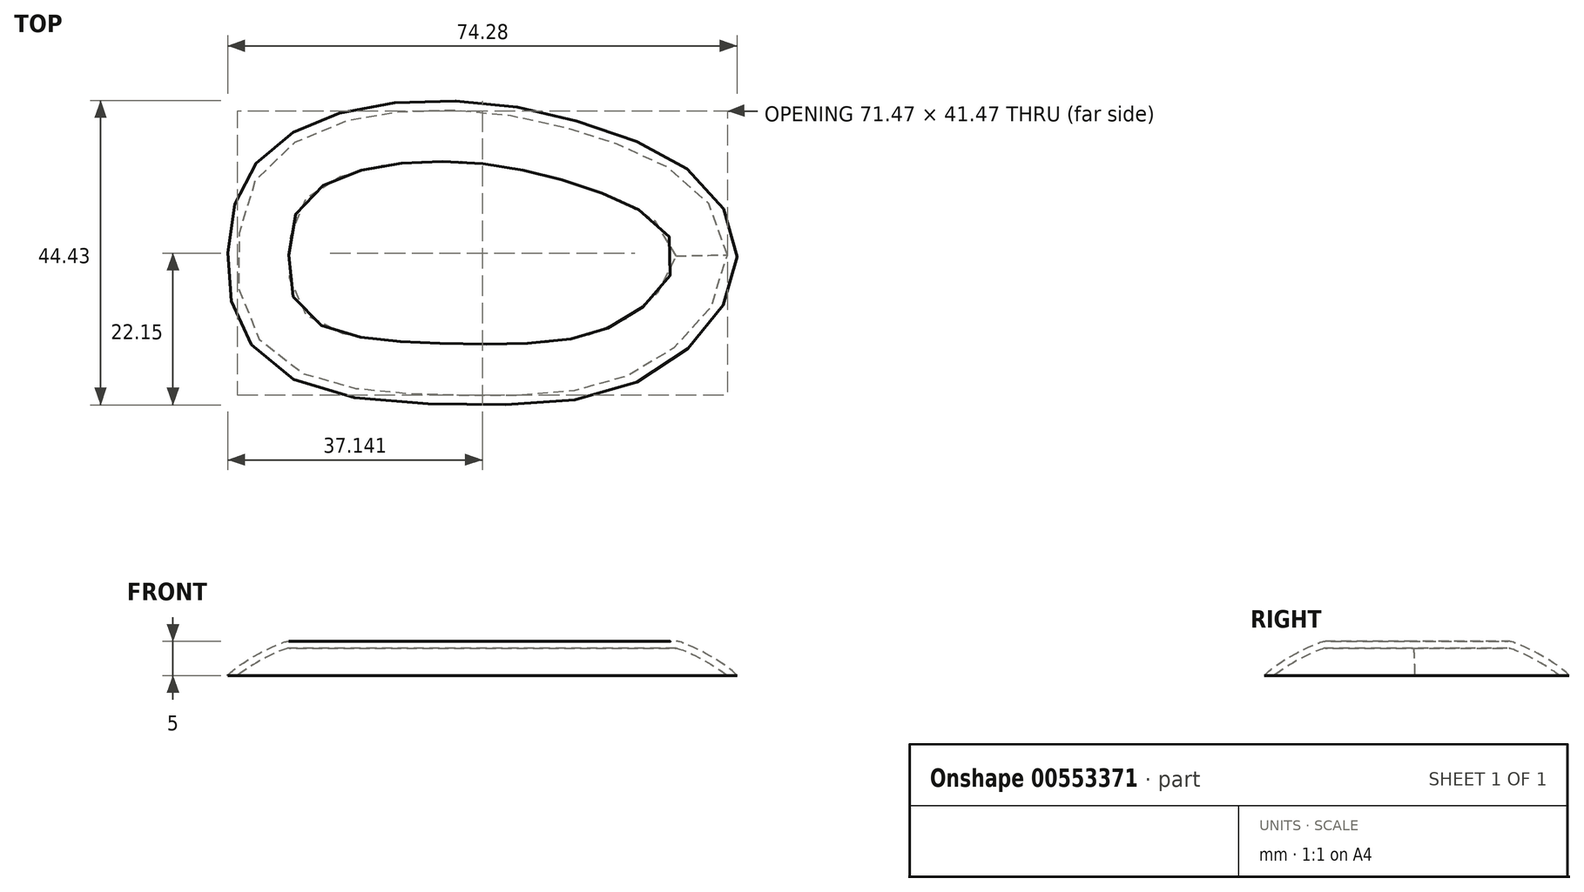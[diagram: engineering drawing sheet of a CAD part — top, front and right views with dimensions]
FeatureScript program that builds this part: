
annotation { "Feature Type Name" : "Feature", "Feature Type Description" : "" }
export const myFeature = defineFeature(function(context is Context, id is Id, definition is map)
    precondition{}
    {
        {
            var Q0;
            Q0=qCreatedBy(makeId("Top.planeOp"),FACE);
            var sketch = newSketch(context, id + "F0", { "sketchPlane" : qUnion([Q0])});
            skFitSpline(sketch, "E0", {"points": [v(0, 0) * mm, v(2.22, 10.29) * mm, v(9.49, 17.56) * mm, v(21.2, 21.46) * mm, v(38.04, 21.82) * mm, v(55.07, 17.91) * mm, v(68.9, 10.64) * mm, v(74.23, 0) * mm, v(69.97, -11) * mm, v(56.14, -20.22) * mm, v(33.61, -22.17) * mm, v(10.9, -19.16) * mm, v(1.5, -10.29) * mm, v(0, 0) * mm]});
            skSolve(sketch);
        }
        {
            var Q0;
            Q0=makeQuery(id+"F0.imprint","IMPRINT",FACE,{"disambiguationData":[TD([[makeQuery(id+"F0.imprint","IMPRINT",EDGE,{"derivedFrom":sQuery(id+"F0.wireOp",EDGE,"E0")}),-1.0]])]});
            extrude(context, id + "F1", {"entities" : qUnion([Q0]), "depth" : 5 * mm, "offsetDistance" : 25 * mm});
        }
        {
            var Q0;
            Q0=makeQuery(id+"F1.opExtrude","CAP_EDGE",EDGE,{"disambiguationData":[OSD([sQuery(id+"F0.wireOp",EDGE,"E0")])],"isStart":false});
            fillet(context, id + "F2", {"entities" : qUnion([Q0]), "radius" : 10.38 * mm, "tangentPropagation" : true, "rho" : 0.2, "crossSection" : FilletCrossSection.CONIC, "allowEdgeOverflow" : false});
        }
        {
            var Q0;
            Q0=makeQuery(id+"F1.opExtrude","CAP_FACE",FACE,{"disambiguationData":[OSD([sQuery(id+"F0.wireOp",EDGE,"E0")])],"isStart":true});
            shell(context, id + "F3", {"entities" : qUnion([Q0]), "thickness" : 1 * mm});
        }
        {
            var Q0;
            Q0=makeQuery(id+"F1.opExtrude","SWEPT_BODY",BODY,{"disambiguationData":[OSD([sQuery(id+"F0.wireOp",EDGE,"E0")])]});
            transform(context, id + "F4", {"entities" : qUnion([Q0]), "transformType" : TransformType.TRANSLATION_3D, "dx" : 0 * mm, "dy" : 0 * mm, "dz" : 0 * mm, "makeCopy" : true});
        }
    });
